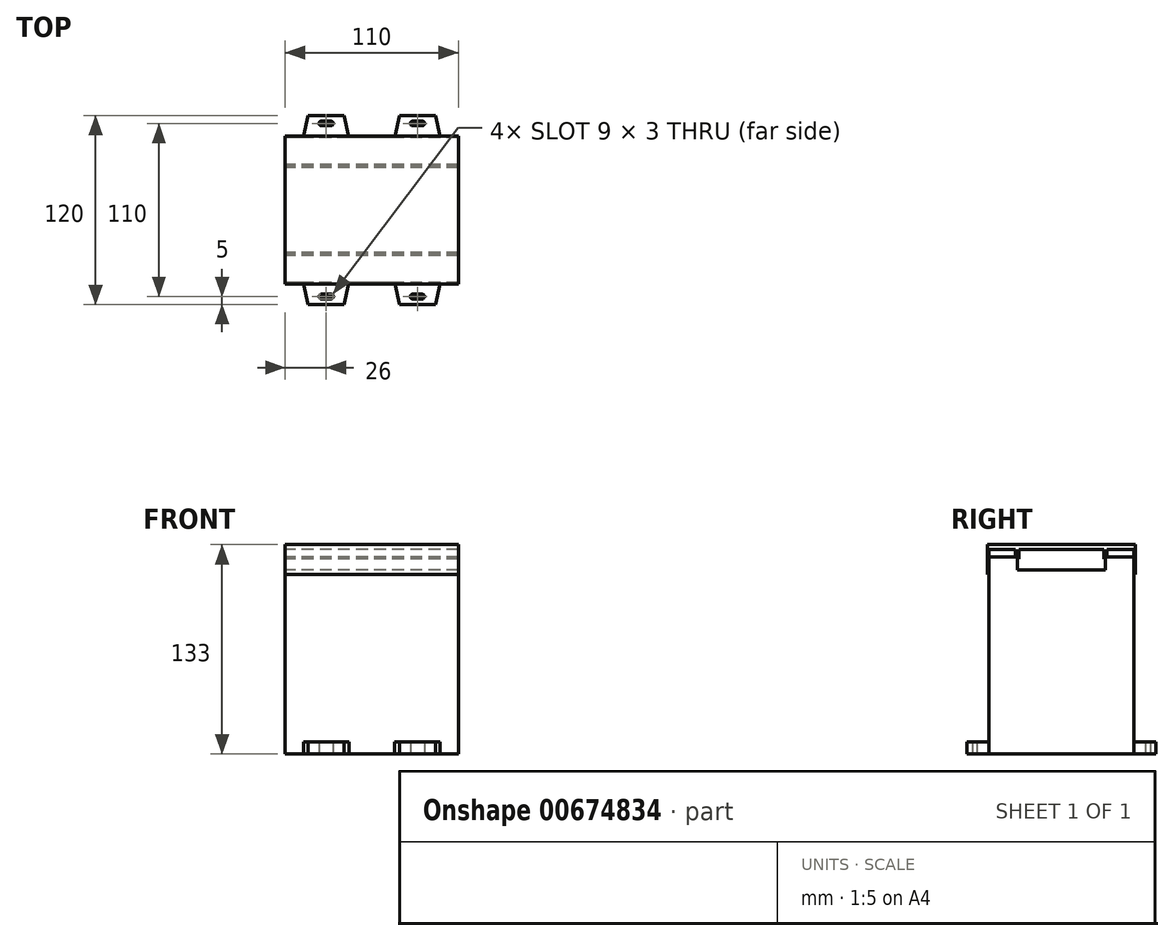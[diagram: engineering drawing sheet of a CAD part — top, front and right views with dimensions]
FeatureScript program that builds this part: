
annotation { "Feature Type Name" : "Feature", "Feature Type Description" : "" }
export const myFeature = defineFeature(function(context is Context, id is Id, definition is map)
    precondition{}
    {
        {
            var Q0;
            Q0=qCreatedBy(makeId("Right.planeOp"),FACE);
            var sketch = newSketch(context, id + "F0", { "sketchPlane" : qUnion([Q0])});
            skLineSegment(sketch, "E0.bottom", {"start": v(-57, 46) * mm, "end": v(57, 46) * mm});
            skLineSegment(sketch, "E0.top", {"start": v(-57, -46) * mm, "end": v(57, -46) * mm});
            skLineSegment(sketch, "E0.left", {"start": v(-57, 46) * mm, "end": v(-57, -46) * mm});
            skLineSegment(sketch, "E0.right", {"start": v(57, 46) * mm, "end": v(57, -46) * mm});
            skPoint(sketch, "E0.middle", {"position": v(0, 0) * mm});
            skLineSegment(sketch, "E1.bottom", {"start": v(-57, 46) * mm, "end": v(-68, 46) * mm});
            skLineSegment(sketch, "E1.top", {"start": v(-57, -46) * mm, "end": v(-68, -46) * mm});
            skLineSegment(sketch, "E1.right", {"start": v(-68, 46) * mm, "end": v(-68, 28) * mm});
            skLineSegment(sketch, "E2.bottom", {"start": v(-68, 46) * mm, "end": v(-57, 46) * mm});
            skLineSegment(sketch, "E2.top", {"start": v(-68, 28) * mm, "end": v(-60, 28) * mm});
            skLineSegment(sketch, "E2.right", {"start": v(-57, 46) * mm, "end": v(-57, 28) * mm});
            skLineSegment(sketch, "E3.bottom", {"start": v(-68, -46) * mm, "end": v(-57, -46) * mm});
            skLineSegment(sketch, "E3.top", {"start": v(-68, -28) * mm, "end": v(-60, -28) * mm});
            skLineSegment(sketch, "E3.left", {"start": v(-68, -46) * mm, "end": v(-68, -28) * mm});
            skLineSegment(sketch, "E3.right", {"start": v(-57, -46) * mm, "end": v(-57, -28) * mm});
            skLineSegment(sketch, "E4", {"start": v(-60, 28) * mm, "end": v(-60, -28) * mm});
            skLineSegment(sketch, "E5.trimOffspring", {"start": v(-68, -28) * mm, "end": v(-68, -46) * mm});
            skLineSegment(sketch, "E6", {"start": v(-73, 46) * mm, "end": v(-73, 29) * mm});
            skLineSegment(sketch, "E7", {"start": v(-57, 46) * mm, "end": v(-73, 46) * mm});
            skLineSegment(sketch, "E8", {"start": v(-57, -46) * mm, "end": v(-73, -46) * mm});
            skLineSegment(sketch, "E9.bottom", {"start": v(-73, 29) * mm, "end": v(-68, 29) * mm});
            skLineSegment(sketch, "E9.top", {"start": v(-73, 27) * mm, "end": v(-67, 27) * mm});
            skLineSegment(sketch, "E9.right", {"start": v(-67, 28) * mm, "end": v(-67, 27) * mm});
            skLineSegment(sketch, "E10.bottom", {"start": v(-73, -27) * mm, "end": v(-67, -27) * mm});
            skLineSegment(sketch, "E10.top", {"start": v(-73, -29) * mm, "end": v(-68, -29) * mm});
            skLineSegment(sketch, "E10.right", {"start": v(-67, -27) * mm, "end": v(-67, -28) * mm});
            skPoint(sketch, "E11.orphan", {"position": v(-67, -29) * mm});
            skLineSegment(sketch, "E12.trimOffspring", {"start": v(-73, 27) * mm, "end": v(-73, -27) * mm});
            skLineSegment(sketch, "E13.0", {"start": v(-76, 16.02) * mm, "end": v(-76, -47) * mm});
            skLineSegment(sketch, "E13.1", {"start": v(-76, 18.02) * mm, "end": v(-76, 16.02) * mm});
            skLineSegment(sketch, "E13.2", {"start": v(-76, 46) * mm, "end": v(-76, 18.02) * mm});
            skLineSegment(sketch, "E14.0", {"start": v(-57, 47) * mm, "end": v(-73, 47) * mm});
            skLineSegment(sketch, "E15.0", {"start": v(-57, -47) * mm, "end": v(-73, -47) * mm});
            skLineSegment(sketch, "E16", {"start": v(-73, 47) * mm, "end": v(-76, 47) * mm});
            skLineSegment(sketch, "E17", {"start": v(-76, 47) * mm, "end": v(-76, 46) * mm});
            skLineSegment(sketch, "E18", {"start": v(-57, 47) * mm, "end": v(-57, 46) * mm});
            skLineSegment(sketch, "E19.trimOffspring", {"start": v(-73, -29) * mm, "end": v(-73, -46) * mm});
            skLineSegment(sketch, "E20", {"start": v(-57, -47) * mm, "end": v(-57, -46) * mm});
            skLineSegment(sketch, "E21", {"start": v(-76, -47) * mm, "end": v(-73, -47) * mm});
            skSolve(sketch);
        }
        {
            var Q0;
            Q0=makeQuery(id+"F0.imprint","IMPRINT",FACE,{"disambiguationData":[TD([[makeQuery(id+"F0.imprint","IMPRINT",EDGE,{"derivedFrom":sQuery(id+"F0.wireOp",EDGE,"E0.bottom")}),-1.0]])]});
            var Q1;
            Q1=makeQuery(id+"F0.imprint","IMPRINT",FACE,{"disambiguationData":[TD([[makeQuery(id+"F0.imprint","IMPRINT",EDGE,{"derivedFrom":sQuery(id+"F0.wireOp",EDGE,"E0.left")}),-1.0]])]});
            extrude(context, id + "F1", {"entities" : qUnion([Q0, Q1]), "depth" : 110 * mm, "offsetDistance" : 25 * mm, "symmetric" : true});
        }
        {
            var Q0;
            Q0=makeQuery(id+"F1.opExtrude","SWEPT_FACE",FACE,{"disambiguationData":[OSD([sQuery(id+"F0.wireOp",EDGE,"E0.right")])]});
            var sketch = newSketch(context, id + "F2", { "sketchPlane" : qUnion([Q0])});
            skLineSegment(sketch, "E22.bottom", {"start": v(32, 56.5) * mm, "end": v(26, 56.5) * mm});
            skLineSegment(sketch, "E22.top", {"start": v(32, 53.5) * mm, "end": v(26, 53.5) * mm});
            skPoint(sketch, "E22.middle", {"position": v(29, 55) * mm});
            skLineSegment(sketch, "E23.bottom", {"start": v(-26, 56.5) * mm, "end": v(-32, 56.5) * mm});
            skLineSegment(sketch, "E23.top", {"start": v(-26, 53.5) * mm, "end": v(-32, 53.5) * mm});
            skPoint(sketch, "E23.middle", {"position": v(-29, 55) * mm});
            skLineSegment(sketch, "E24.bottom", {"start": v(32, -53.5) * mm, "end": v(26, -53.5) * mm});
            skLineSegment(sketch, "E24.top", {"start": v(32, -56.5) * mm, "end": v(26, -56.5) * mm});
            skPoint(sketch, "E24.middle", {"position": v(29, -55) * mm});
            skLineSegment(sketch, "E25.bottom", {"start": v(-26, -53.5) * mm, "end": v(-32, -53.5) * mm});
            skLineSegment(sketch, "E25.top", {"start": v(-26, -56.5) * mm, "end": v(-32, -56.5) * mm});
            skPoint(sketch, "E25.middle", {"position": v(-29, -55) * mm});
            skLineSegment(sketch, "E26.bottom", {"start": v(17.5, 60) * mm, "end": v(40.5, 60) * mm});
            skLineSegment(sketch, "E26.top", {"start": v(14.5, 46) * mm, "end": v(43.5, 46) * mm});
            skLineSegment(sketch, "E27", {"start": v(40.5, 60) * mm, "end": v(43.5, 46) * mm});
            skPoint(sketch, "E28.orphan", {"position": v(43.5, 60) * mm});
            skPoint(sketch, "E29", {"position": v(17.5, 60) * mm});
            skLineSegment(sketch, "E30", {"start": v(17.5, 60) * mm, "end": v(14.5, 46) * mm});
            skPoint(sketch, "E31.orphan", {"position": v(14.5, 60) * mm});
            skArc(sketch, "E32", {"start": v(32, 53.5) * mm, "mid": v(33.5, 55) * mm, "end": v(32, 56.5) * mm});
            skArc(sketch, "E33", {"start": v(26, 56.5) * mm, "mid": v(24.5, 55) * mm, "end": v(26, 53.5) * mm});
            skLineSegment(sketch, "E34.bottom", {"start": v(-40.5, 60) * mm, "end": v(-17.5, 60) * mm});
            skLineSegment(sketch, "E34.top", {"start": v(-43.5, 46) * mm, "end": v(-14.5, 46) * mm});
            skPoint(sketch, "E35", {"position": v(-17.5, 60) * mm});
            skPoint(sketch, "E36", {"position": v(-40.5, 60) * mm});
            skLineSegment(sketch, "E37", {"start": v(-17.5, 60) * mm, "end": v(-14.5, 46) * mm});
            skLineSegment(sketch, "E38", {"start": v(-40.5, 60) * mm, "end": v(-43.5, 46) * mm});
            skPoint(sketch, "E34.right.start.orphan", {"position": v(-14.5, 60) * mm});
            skPoint(sketch, "E34.left.start.orphan", {"position": v(-43.5, 60) * mm});
            skArc(sketch, "E39", {"start": v(-26, 53.5) * mm, "mid": v(-24.5, 55) * mm, "end": v(-26, 56.5) * mm});
            skArc(sketch, "E40", {"start": v(-32, 56.5) * mm, "mid": v(-33.5, 55) * mm, "end": v(-32, 53.5) * mm});
            skLineSegment(sketch, "E41.bottom", {"start": v(14.5, -46) * mm, "end": v(43.5, -46) * mm});
            skLineSegment(sketch, "E41.top", {"start": v(17.5, -60) * mm, "end": v(40.5, -60) * mm});
            skLineSegment(sketch, "E42.bottom", {"start": v(-43.5, -46) * mm, "end": v(-14.5, -46) * mm});
            skLineSegment(sketch, "E42.top", {"start": v(-40.5, -60) * mm, "end": v(-17.5, -60) * mm});
            skPoint(sketch, "E43", {"position": v(40.5, -60) * mm});
            skPoint(sketch, "E44", {"position": v(17.5, -60) * mm});
            skPoint(sketch, "E45", {"position": v(-17.5, -60) * mm});
            skPoint(sketch, "E46", {"position": v(-40.5, -60) * mm});
            skLineSegment(sketch, "E47", {"start": v(43.5, -46) * mm, "end": v(40.5, -60) * mm});
            skLineSegment(sketch, "E48", {"start": v(14.5, -46) * mm, "end": v(17.5, -60) * mm});
            skLineSegment(sketch, "E49", {"start": v(-17.5, -60) * mm, "end": v(-14.5, -46) * mm});
            skLineSegment(sketch, "E50", {"start": v(-43.5, -46) * mm, "end": v(-40.5, -60) * mm});
            skPoint(sketch, "E42.right.end.orphan", {"position": v(-14.5, -60) * mm});
            skPoint(sketch, "E42.left.end.orphan", {"position": v(-43.5, -60) * mm});
            skPoint(sketch, "E51.orphan", {"position": v(43.5, -60) * mm});
            skPoint(sketch, "E41.left.end.orphan", {"position": v(14.5, -60) * mm});
            skArc(sketch, "E52", {"start": v(32, -56.5) * mm, "mid": v(33.5, -55) * mm, "end": v(32, -53.5) * mm});
            skArc(sketch, "E53", {"start": v(26, -53.5) * mm, "mid": v(24.5, -55) * mm, "end": v(26, -56.5) * mm});
            skArc(sketch, "E54", {"start": v(-26, -56.5) * mm, "mid": v(-24.5, -55) * mm, "end": v(-26, -53.5) * mm});
            skArc(sketch, "E55", {"start": v(-32, -53.5) * mm, "mid": v(-33.5, -55) * mm, "end": v(-32, -56.5) * mm});
            skSolve(sketch);
        }
        {
            var Q0;
            Q0=makeQuery(id+"F2.imprint","IMPRINT",FACE,{"disambiguationData":[TD([[makeQuery(id+"F2.imprint","IMPRINT",EDGE,{"derivedFrom":sQuery(id+"F2.wireOp",EDGE,"E23.bottom")}),-1.0]])]});
            var Q1;
            Q1=makeQuery(id+"F2.imprint","IMPRINT",FACE,{"disambiguationData":[TD([[makeQuery(id+"F2.imprint","IMPRINT",EDGE,{"derivedFrom":sQuery(id+"F2.wireOp",EDGE,"E22.bottom")}),-1.0]])]});
            var Q2;
            Q2=makeQuery(id+"F2.imprint","IMPRINT",FACE,{"disambiguationData":[TD([[makeQuery(id+"F2.imprint","IMPRINT",EDGE,{"derivedFrom":sQuery(id+"F2.wireOp",EDGE,"E25.bottom")}),-1.0]])]});
            var Q3;
            Q3=makeQuery(id+"F2.imprint","IMPRINT",FACE,{"disambiguationData":[TD([[makeQuery(id+"F2.imprint","IMPRINT",EDGE,{"derivedFrom":sQuery(id+"F2.wireOp",EDGE,"E24.bottom")}),-1.0]])]});
            extrude(context, id + "F3", {"entities" : qUnion([Q0, Q1, Q2, Q3]), "operationType" : NewBodyOperationType.ADD, "oppositeDirection" : true, "depth" : 7.5 * mm, "offsetDistance" : 25 * mm});
        }
        {
            var Q0;
            {var subQ13=sQuery(id+"F0.wireOp",EDGE,"E6");Q0=makeQuery(id+"F0.imprint","IMPRINT",FACE,{"disambiguationData":[TD([[makeQuery(id+"F0.imprint","IMPRINT",EDGE,{"derivedFrom":subQ13}),-1.0]])]});}
            extrude(context, id + "F4", {"entities" : qUnion([Q0]), "depth" : 110 * mm, "offsetDistance" : 25 * mm, "symmetric" : true});
        }
        {
            var Q0;
            Q0=makeQuery(id+"F1.opExtrude","SWEPT_BODY",BODY,{"disambiguationData":[OSD([sQuery(id+"F0.wireOp",EDGE,"E0.bottom"),sQuery(id+"F0.wireOp",EDGE,"E0.top"),sQuery(id+"F0.wireOp",EDGE,"E0.right"),sQuery(id+"F0.wireOp",EDGE,"E2.top"),sQuery(id+"F0.wireOp",EDGE,"E1.right"),sQuery(id+"F0.wireOp",EDGE,"E3.top"),sQuery(id+"F0.wireOp",EDGE,"E4"),sQuery(id+"F0.wireOp",EDGE,"E5.trimOffspring"),sQuery(id+"F0.wireOp",EDGE,"E7"),sQuery(id+"F0.wireOp",EDGE,"E8")])]});
            var Q1;
            Q1=makeQuery(id+"F4.opExtrude","SWEPT_BODY",BODY,{"disambiguationData":[OSD([sQuery(id+"F0.wireOp",EDGE,"E2.top"),sQuery(id+"F0.wireOp",EDGE,"E1.right"),sQuery(id+"F0.wireOp",EDGE,"E3.top"),sQuery(id+"F0.wireOp",EDGE,"E5.trimOffspring"),sQuery(id+"F0.wireOp",EDGE,"E6"),sQuery(id+"F0.wireOp",EDGE,"E7"),sQuery(id+"F0.wireOp",EDGE,"E8"),sQuery(id+"F0.wireOp",EDGE,"E9.bottom"),sQuery(id+"F0.wireOp",EDGE,"E9.top"),sQuery(id+"F0.wireOp",EDGE,"E9.right"),sQuery(id+"F0.wireOp",EDGE,"E10.bottom"),sQuery(id+"F0.wireOp",EDGE,"E10.top"),sQuery(id+"F0.wireOp",EDGE,"E10.right"),sQuery(id+"F0.wireOp",EDGE,"E12.trimOffspring"),sQuery(id+"F0.wireOp",EDGE,"E13.0"),sQuery(id+"F0.wireOp",EDGE,"E13.1"),sQuery(id+"F0.wireOp",EDGE,"E13.2"),sQuery(id+"F0.wireOp",EDGE,"E14.0"),sQuery(id+"F0.wireOp",EDGE,"E15.0"),sQuery(id+"F0.wireOp",EDGE,"E16"),sQuery(id+"F0.wireOp",EDGE,"E17"),sQuery(id+"F0.wireOp",EDGE,"E18"),sQuery(id+"F0.wireOp",EDGE,"E19.trimOffspring"),sQuery(id+"F0.wireOp",EDGE,"E20"),sQuery(id+"F0.wireOp",EDGE,"E21")])]});
            var Q2;
            {var subQ1=sQuery(id+"F2.wireOp",EDGE,"E30");var subQ2=sQuery(id+"F0.wireOp",EDGE,"E0.bottom");var subQ3=sQuery(id+"F0.wireOp",EDGE,"E0.right");Q2=makeQuery(id+"F3.boolean.opBoolean","SPLIT",EDGE,{"disambiguationData":[TD([makeQuery(id+"F3.opExtrude","SWEPT_FACE",FACE,{"disambiguationData":[OSD([subQ1])]})])],"derivedFrom":makeQuery(id+"F1.opExtrude","SWEPT_EDGE",EDGE,{"disambiguationData":[OSD([subQ2,subQ3])]})});}
            transform(context, id + "F5", {"entities" : qUnion([Q0, Q1]), "transformType" : TransformType.ROTATION, "transformAxis" : qUnion([Q2]), "angle" : 90 * degree, "makeCopy" : false});
        }
    });
